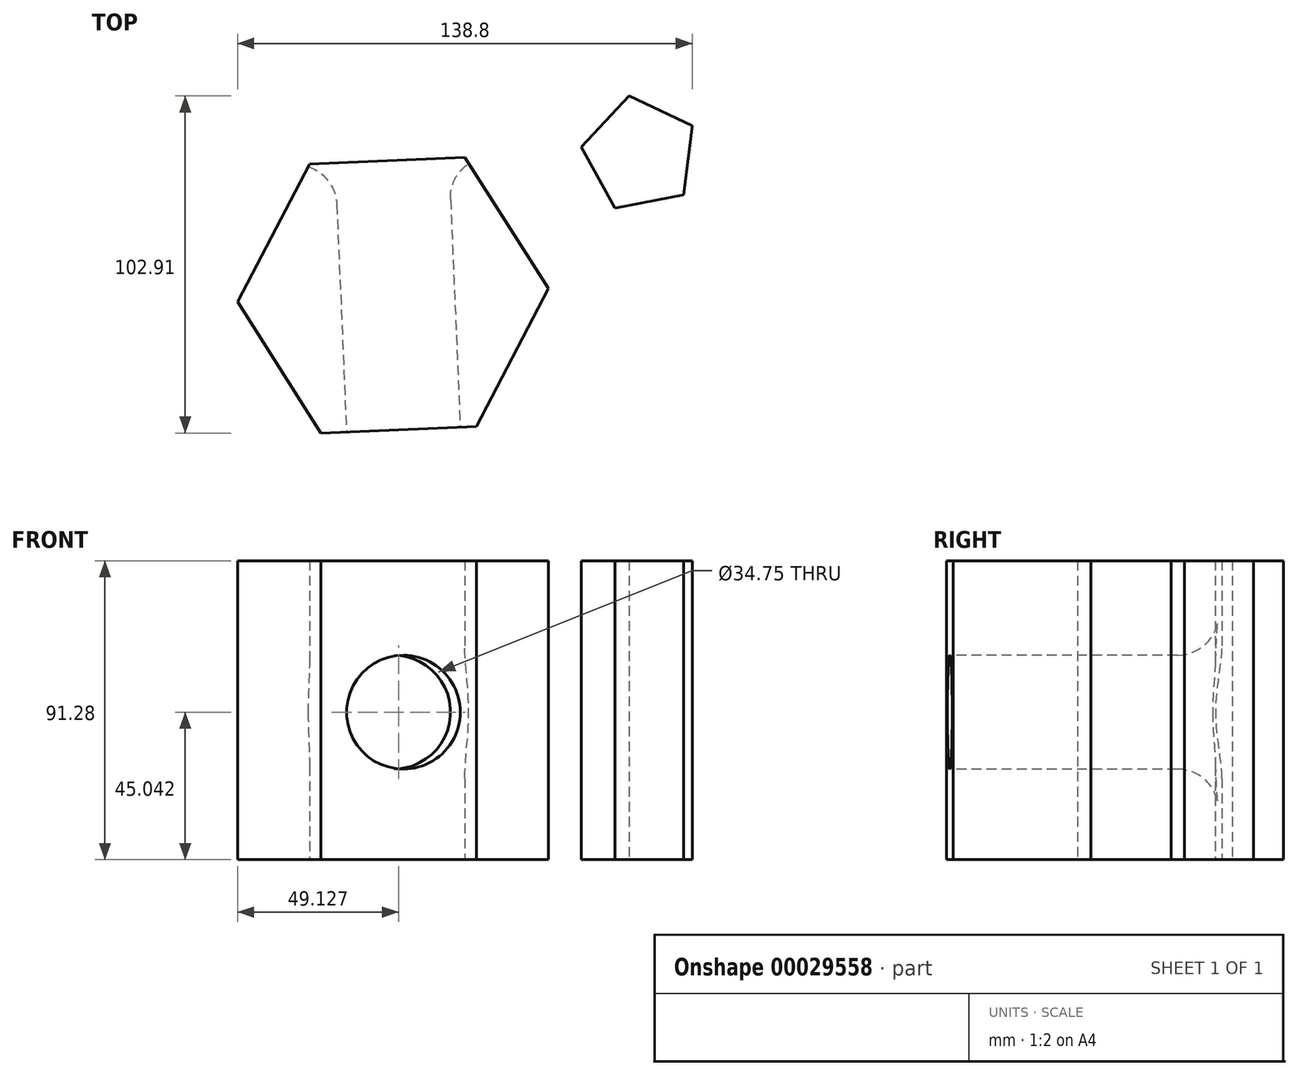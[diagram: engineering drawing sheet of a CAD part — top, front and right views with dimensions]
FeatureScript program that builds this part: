
annotation { "Feature Type Name" : "Feature", "Feature Type Description" : "" }
export const myFeature = defineFeature(function(context is Context, id is Id, definition is map)
    precondition{}
    {
        {
            var Q0;
            Q0=qCreatedBy(makeId("Top.planeOp"),FACE);
            var sketch = newSketch(context, id + "F0", { "sketchPlane" : qUnion([Q0])});
            skCircle(sketch, "E0.cCircle", {"center": v(-29.4, 0) * mm, "radius": 47.46 * mm, "construction": true});
            skLineSegment(sketch, "E0.0", {"start": v(-76.8, -2.03) * mm, "end": v(-54.86, 40.04) * mm});
            skLineSegment(sketch, "E0.1", {"start": v(-54.86, 40.04) * mm, "end": v(-7.45, 42.08) * mm});
            skLineSegment(sketch, "E0.2", {"start": v(-7.45, 42.08) * mm, "end": v(18.02, 2.03) * mm});
            skLineSegment(sketch, "E0.3", {"start": v(18.02, 2.03) * mm, "end": v(-3.92, -40.04) * mm});
            skLineSegment(sketch, "E0.4", {"start": v(-3.92, -40.04) * mm, "end": v(-51.34, -42.08) * mm});
            skLineSegment(sketch, "E0.5", {"start": v(-51.34, -42.08) * mm, "end": v(-76.8, -2.03) * mm});
            skCircle(sketch, "E1.cCircle", {"center": v(46.1, 43.02) * mm, "radius": 18.14 * mm, "construction": true});
            skLineSegment(sketch, "E1.0", {"start": v(62, 51.76) * mm, "end": v(59.32, 30.6) * mm});
            skLineSegment(sketch, "E1.1", {"start": v(59.32, 30.6) * mm, "end": v(38.38, 26.61) * mm});
            skLineSegment(sketch, "E1.2", {"start": v(38.38, 26.61) * mm, "end": v(28.11, 45.3) * mm});
            skLineSegment(sketch, "E1.3", {"start": v(28.11, 45.3) * mm, "end": v(42.7, 60.83) * mm});
            skLineSegment(sketch, "E1.4", {"start": v(42.7, 60.83) * mm, "end": v(62, 51.76) * mm});
            skSolve(sketch);
        }
        {
            var Q0;
            Q0 = qSketchRegion(id + "F0", true);
            var Q1;
            Q1 = qBodyType(qCreatedBy(id + "F0" ,EDGE), BodyType.WIRE);
            extrude(context, id + "F1", {"entities" : qUnion([Q0]), "surfaceEntities" : qUnion([Q1]), "depth" : 91.28 * mm});
        }
        {
            var Q0;
            Q0=makeQuery(id+"F1.opExtrude","SWEPT_FACE",FACE,{"disambiguationData":[OSD([sQuery(id+"F0.wireOp",EDGE,"E0.4")])]});
            var sketch = newSketch(context, id + "F2", { "sketchPlane" : qUnion([Q0])});
            skCircle(sketch, "E2", {"center": v(-27.93, 45.04) * mm, "radius": 17.37 * mm});
            skSolve(sketch);
        }
        {
            var Q0;
            Q0 = qSketchRegion(id + "F2", true);
            var Q1;
            Q1 = qBodyType(qCreatedBy(id + "F2" ,EDGE), BodyType.WIRE);
            extrude(context, id + "F3", {"entities" : qUnion([Q0]), "operationType" : NewBodyOperationType.REMOVE, "surfaceEntities" : qUnion([Q1]), "oppositeDirection" : true, "depth" : 104.73 * mm});
        }
        {
            var Q0;
            Q0=makeQuery(id+"F3.boolean.opBoolean","INTERSECT",EDGE,{"derivedFrom":[makeQuery(id+"F1.opExtrude","SWEPT_FACE",FACE,{"disambiguationData":[OSD([sQuery(id+"F0.wireOp",EDGE,"E0.1")])]}),makeQuery(id+"F3.opExtrude","SWEPT_FACE",FACE,{"disambiguationData":[OSD([sQuery(id+"F2.wireOp",EDGE,"E2")])]})]});
            fillet(context, id + "F4", {"entities" : qUnion([Q0]), "radius" : 12.7 * mm, "tangentPropagation" : true, "allowEdgeOverflow" : false});
        }
    });
